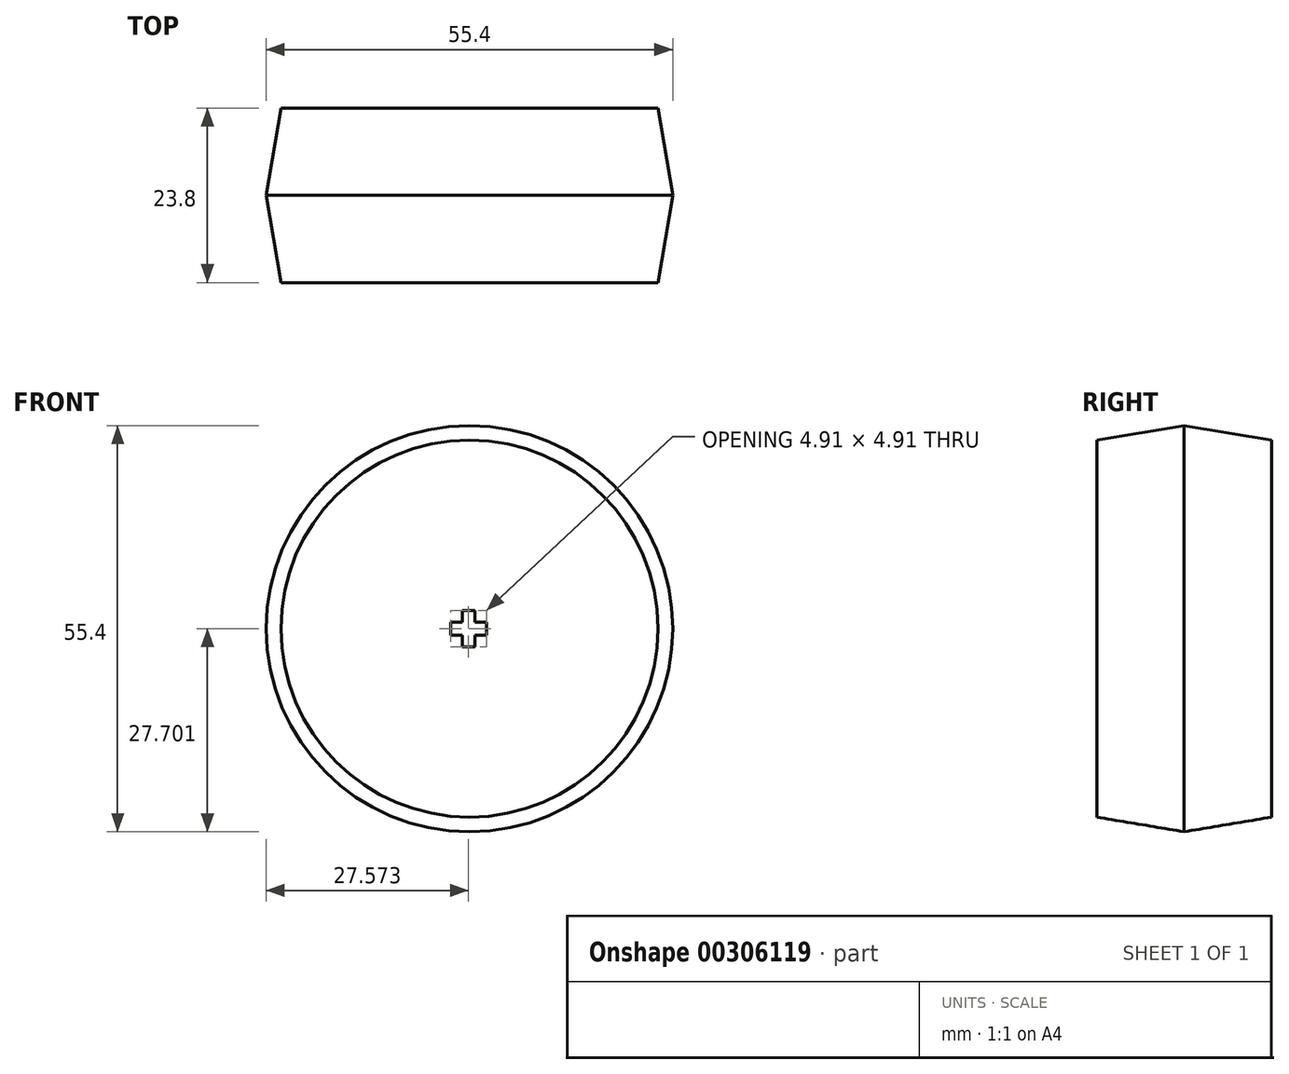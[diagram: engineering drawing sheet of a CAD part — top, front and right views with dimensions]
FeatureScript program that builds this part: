
annotation { "Feature Type Name" : "Feature", "Feature Type Description" : "" }
export const myFeature = defineFeature(function(context is Context, id is Id, definition is map)
    precondition{}
    {
        {
            var Q0;
            Q0=qCreatedBy(makeId("Front.planeOp"),FACE);
            var sketch = newSketch(context, id + "F0", { "sketchPlane" : qUnion([Q0])});
            skCircle(sketch, "E0", {"center": v(0.36, 0) * mm, "radius": 27.7 * mm});
            skLineSegment(sketch, "E1", {"start": v(0.36, 0) * mm, "end": v(-2.22, 0) * mm});
            skLineSegment(sketch, "E2", {"start": v(-2.22, 0) * mm, "end": v(-2.22, -0.87) * mm});
            skLineSegment(sketch, "E3", {"start": v(-2.22, -0.87) * mm, "end": v(-0.64, -0.87) * mm});
            skLineSegment(sketch, "E4", {"start": v(-0.64, -0.87) * mm, "end": v(-0.64, -2.45) * mm});
            skLineSegment(sketch, "E5", {"start": v(-0.64, -2.45) * mm, "end": v(1.1, -2.45) * mm});
            skLineSegment(sketch, "E6", {"start": v(1.1, -2.45) * mm, "end": v(1.1, -0.87) * mm});
            skLineSegment(sketch, "E7", {"start": v(1.1, -0.87) * mm, "end": v(2.69, -0.87) * mm});
            skLineSegment(sketch, "E8", {"start": v(2.69, -0.87) * mm, "end": v(2.69, 0.88) * mm});
            skLineSegment(sketch, "E9", {"start": v(2.69, 0.88) * mm, "end": v(1.1, 0.88) * mm});
            skLineSegment(sketch, "E10", {"start": v(1.1, 0.88) * mm, "end": v(1.1, 2.46) * mm});
            skLineSegment(sketch, "E11", {"start": v(1.1, 2.46) * mm, "end": v(-0.64, 2.46) * mm});
            skLineSegment(sketch, "E12", {"start": v(-0.64, 2.46) * mm, "end": v(-0.64, 0.88) * mm});
            skLineSegment(sketch, "E13", {"start": v(-0.64, 0.88) * mm, "end": v(-2.22, 0.88) * mm});
            skLineSegment(sketch, "E14", {"start": v(-2.22, 0.88) * mm, "end": v(-2.22, 0) * mm});
            skSolve(sketch);
        }
        {
            var Q0;
            Q0=makeQuery(id+"F0.imprint","IMPRINT",FACE,{"disambiguationData":[TD([[makeQuery(id+"F0.imprint","IMPRINT",EDGE,{"derivedFrom":sQuery(id+"F0.wireOp",EDGE,"E0")}),1.0]])]});
            extrude(context, id + "F1", {"entities" : qUnion([Q0]), "depth" : 23.8 * mm});
        }
        {
            var Q0;
            Q0=makeQuery(id+"F1.opExtrude","CAP_EDGE",EDGE,{"disambiguationData":[OSD([sQuery(id+"F0.wireOp",EDGE,"E0")])],"isStart":false});
            var Q1;
            Q1=makeQuery(id+"F1.opExtrude","CAP_EDGE",EDGE,{"disambiguationData":[OSD([sQuery(id+"F0.wireOp",EDGE,"E0")])],"isStart":true});
            chamfer(context, id + "F2", {"entities" : qUnion([Q0, Q1]), "chamferType" : ChamferType.TWO_OFFSETS, "width1" : 2 * mm, "oppositeDirection" : false, "width2" : (23.8 / 2) * mm, "tangentPropagation" : true});
        }
    });
